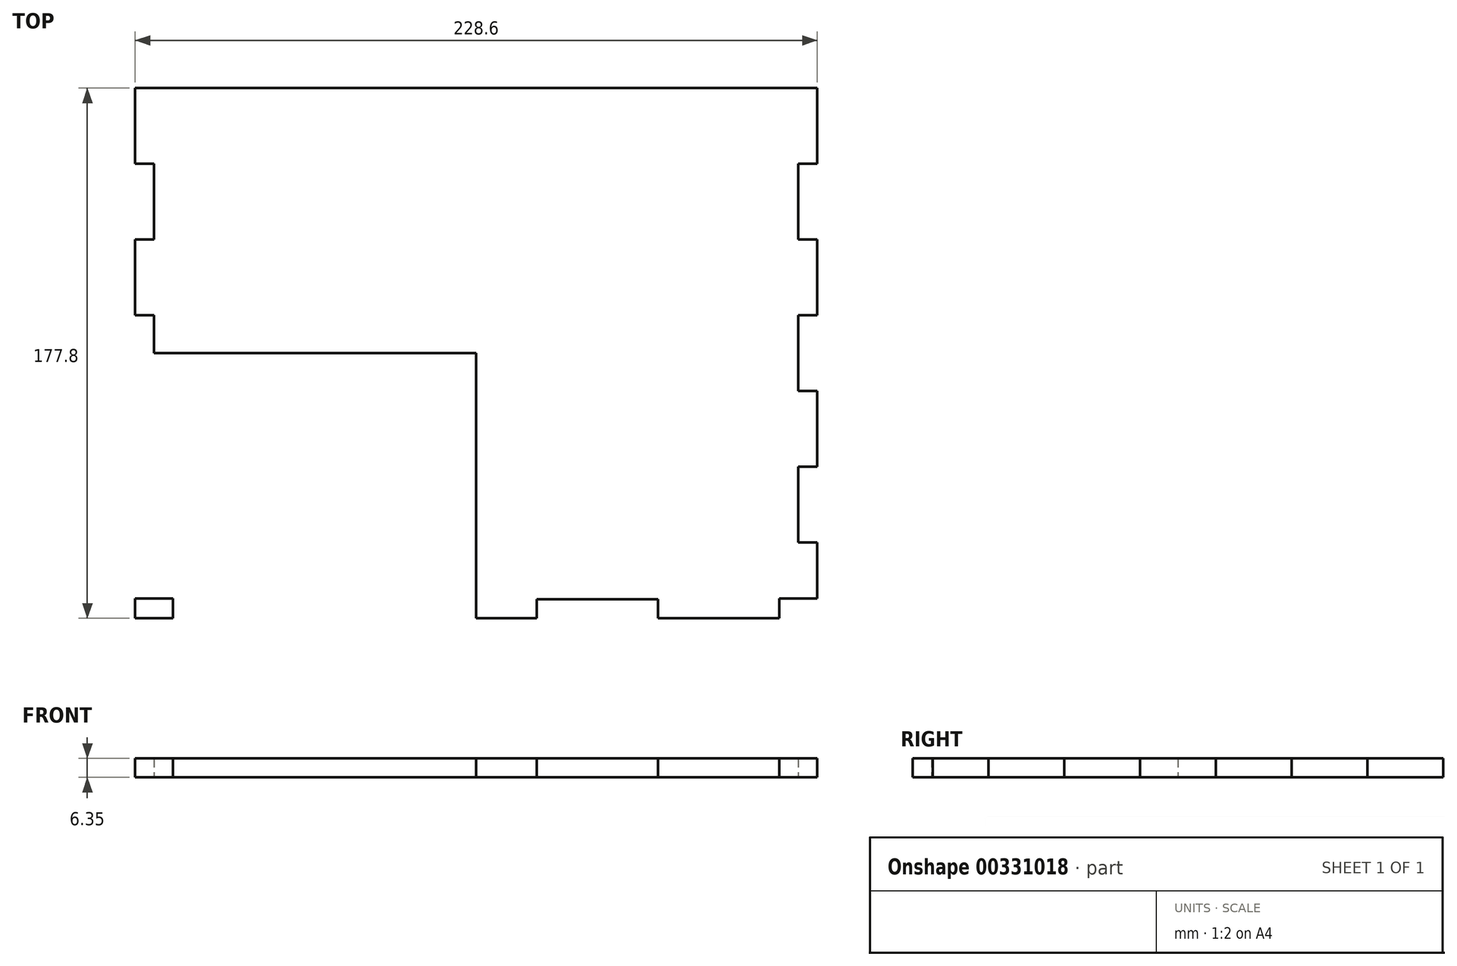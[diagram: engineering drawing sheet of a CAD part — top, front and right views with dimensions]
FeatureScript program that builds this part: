
annotation { "Feature Type Name" : "Feature", "Feature Type Description" : "" }
export const myFeature = defineFeature(function(context is Context, id is Id, definition is map)
    precondition{}
    {
        {
            var Q0;
            Q0=qCreatedBy(makeId("Top.planeOp"),FACE);
            var sketch = newSketch(context, id + "F0", { "sketchPlane" : qUnion([Q0])});
            skLineSegment(sketch, "E0.bottom", {"start": v(114.3, 88.9) * mm, "end": v(-114.3, 88.9) * mm});
            skLineSegment(sketch, "E0.top", {"start": v(114.3, -88.9) * mm, "end": v(-114.3, -88.9) * mm});
            skLineSegment(sketch, "E0.left", {"start": v(114.3, 88.9) * mm, "end": v(114.3, -88.9) * mm});
            skLineSegment(sketch, "E0.right", {"start": v(-114.3, 88.9) * mm, "end": v(-114.3, -88.9) * mm});
            skPoint(sketch, "E0.middle", {"position": v(0, 0) * mm});
            skLineSegment(sketch, "E1", {"start": v(-114.3, 88.9) * mm, "end": v(-114.3, 82.55) * mm});
            skLineSegment(sketch, "E2", {"start": v(-114.3, 88.9) * mm, "end": v(-101.6, 88.9) * mm});
            skLineSegment(sketch, "E3.bottom", {"start": v(-101.6, 88.9) * mm, "end": v(-114.3, 88.9) * mm});
            skLineSegment(sketch, "E3.top", {"start": v(-101.6, 82.55) * mm, "end": v(-114.3, 82.55) * mm});
            skLineSegment(sketch, "E3.left", {"start": v(-101.6, 88.9) * mm, "end": v(-101.6, 82.55) * mm});
            skLineSegment(sketch, "E4", {"start": v(-114.3, 88.9) * mm, "end": v(-114.3, 63.5) * mm});
            skLineSegment(sketch, "E5.bottom", {"start": v(-114.3, 63.5) * mm, "end": v(-107.95, 63.5) * mm});
            skLineSegment(sketch, "E5.top", {"start": v(-114.3, 38.1) * mm, "end": v(-107.95, 38.1) * mm});
            skLineSegment(sketch, "E5.left", {"start": v(-114.3, 63.5) * mm, "end": v(-114.3, 38.1) * mm});
            skLineSegment(sketch, "E5.right", {"start": v(-107.95, 63.5) * mm, "end": v(-107.95, 38.1) * mm});
            skLineSegment(sketch, "E6", {"start": v(-114.3, 38.1) * mm, "end": v(-114.3, 12.7) * mm});
            skLineSegment(sketch, "E7.bottom", {"start": v(-114.3, 12.7) * mm, "end": v(-107.95, 12.7) * mm});
            skLineSegment(sketch, "E7.top", {"start": v(-114.3, -12.7) * mm, "end": v(-107.95, -12.7) * mm});
            skLineSegment(sketch, "E7.left", {"start": v(-114.3, 12.7) * mm, "end": v(-114.3, -12.7) * mm});
            skLineSegment(sketch, "E7.right", {"start": v(-107.95, 12.7) * mm, "end": v(-107.95, -12.7) * mm});
            skLineSegment(sketch, "E8", {"start": v(-114.3, -12.7) * mm, "end": v(-114.3, -38.1) * mm});
            skLineSegment(sketch, "E9.bottom", {"start": v(-114.3, -38.1) * mm, "end": v(-107.95, -38.1) * mm});
            skLineSegment(sketch, "E9.top", {"start": v(-114.3, -63.5) * mm, "end": v(-107.95, -63.5) * mm});
            skLineSegment(sketch, "E9.left", {"start": v(-114.3, -38.1) * mm, "end": v(-114.3, -63.5) * mm});
            skLineSegment(sketch, "E9.right", {"start": v(-107.95, -38.1) * mm, "end": v(-107.95, -63.5) * mm});
            skLineSegment(sketch, "E10", {"start": v(-114.3, -88.9) * mm, "end": v(-114.3, -82.55) * mm});
            skLineSegment(sketch, "E11.bottom", {"start": v(-114.3, -88.9) * mm, "end": v(-101.6, -88.9) * mm});
            skLineSegment(sketch, "E11.top", {"start": v(-114.3, -82.26) * mm, "end": v(-101.6, -82.26) * mm});
            skLineSegment(sketch, "E11.left", {"start": v(-114.3, -88.9) * mm, "end": v(-114.3, -82.26) * mm});
            skLineSegment(sketch, "E11.right", {"start": v(-101.6, -88.9) * mm, "end": v(-101.6, -82.26) * mm});
            skLineSegment(sketch, "E12", {"start": v(0, 88.9) * mm, "end": v(0, -88.9) * mm});
            skLineSegment(sketch, "E13.MirrorCS", {"start": v(101.6, 88.9) * mm, "end": v(114.3, 88.9) * mm});
            skLineSegment(sketch, "E14.MirrorCS", {"start": v(101.6, 88.9) * mm, "end": v(101.6, 82.55) * mm});
            skLineSegment(sketch, "E15.MirrorCS", {"start": v(101.6, 82.55) * mm, "end": v(114.3, 82.55) * mm});
            skLineSegment(sketch, "E16.MirrorCS", {"start": v(114.3, 88.9) * mm, "end": v(114.3, 63.5) * mm});
            skLineSegment(sketch, "E17.MirrorCS", {"start": v(114.3, 63.5) * mm, "end": v(107.95, 63.5) * mm});
            skLineSegment(sketch, "E18.MirrorCS", {"start": v(107.95, 63.5) * mm, "end": v(107.95, 38.1) * mm});
            skLineSegment(sketch, "E19.MirrorCS", {"start": v(114.3, 38.1) * mm, "end": v(107.95, 38.1) * mm});
            skLineSegment(sketch, "E20.MirrorCS", {"start": v(114.3, 12.7) * mm, "end": v(107.95, 12.7) * mm});
            skLineSegment(sketch, "E21.MirrorCS", {"start": v(107.95, 12.7) * mm, "end": v(107.95, -12.7) * mm});
            skLineSegment(sketch, "E22.MirrorCS", {"start": v(114.3, -12.7) * mm, "end": v(107.95, -12.7) * mm});
            skLineSegment(sketch, "E23.MirrorCS", {"start": v(114.3, -38.1) * mm, "end": v(107.95, -38.1) * mm});
            skLineSegment(sketch, "E24.MirrorCS", {"start": v(107.95, -38.1) * mm, "end": v(107.95, -63.5) * mm});
            skLineSegment(sketch, "E25.MirrorCS", {"start": v(114.3, -63.5) * mm, "end": v(107.95, -63.5) * mm});
            skLineSegment(sketch, "E26.MirrorCS", {"start": v(114.3, -82.26) * mm, "end": v(101.6, -82.26) * mm});
            skLineSegment(sketch, "E27.MirrorCS", {"start": v(101.6, -88.9) * mm, "end": v(101.6, -82.26) * mm});
            skLineSegment(sketch, "E28.MirrorCS", {"start": v(-114.3, -88.9) * mm, "end": v(114.3, -88.9) * mm});
            skLineSegment(sketch, "E29", {"start": v(-114.3, 0) * mm, "end": v(114.3, 0) * mm});
            skLineSegment(sketch, "E30", {"start": v(-101.6, 88.9) * mm, "end": v(-60.96, 88.9) * mm});
            skLineSegment(sketch, "E31.bottom", {"start": v(-60.96, 88.9) * mm, "end": v(-20.32, 88.9) * mm});
            skLineSegment(sketch, "E31.top", {"start": v(-60.96, 82.55) * mm, "end": v(-20.32, 82.55) * mm});
            skLineSegment(sketch, "E31.left", {"start": v(-60.96, 88.9) * mm, "end": v(-60.96, 82.55) * mm});
            skLineSegment(sketch, "E31.right", {"start": v(-20.32, 88.9) * mm, "end": v(-20.32, 82.55) * mm});
            skLineSegment(sketch, "E32", {"start": v(-20.32, 88.9) * mm, "end": v(20.32, 88.9) * mm});
            skLineSegment(sketch, "E33.bottom", {"start": v(20.32, 88.9) * mm, "end": v(60.96, 88.9) * mm});
            skLineSegment(sketch, "E33.top", {"start": v(20.32, 82.55) * mm, "end": v(60.96, 82.55) * mm});
            skLineSegment(sketch, "E33.left", {"start": v(20.32, 88.9) * mm, "end": v(20.32, 82.55) * mm});
            skLineSegment(sketch, "E33.right", {"start": v(60.96, 88.9) * mm, "end": v(60.96, 82.55) * mm});
            skLineSegment(sketch, "E34.MirrorCS", {"start": v(-101.6, -88.9) * mm, "end": v(-60.96, -88.9) * mm});
            skLineSegment(sketch, "E35.MirrorCS", {"start": v(-60.96, -88.9) * mm, "end": v(-60.96, -82.55) * mm});
            skLineSegment(sketch, "E36.MirrorCS", {"start": v(-60.96, -88.9) * mm, "end": v(-20.32, -88.9) * mm});
            skLineSegment(sketch, "E37.MirrorCS", {"start": v(-60.96, -82.55) * mm, "end": v(-20.32, -82.55) * mm});
            skLineSegment(sketch, "E38.MirrorCS", {"start": v(-20.32, -88.9) * mm, "end": v(-20.32, -82.55) * mm});
            skLineSegment(sketch, "E39.MirrorCS", {"start": v(20.32, -82.55) * mm, "end": v(60.96, -82.55) * mm});
            skLineSegment(sketch, "E40.MirrorCS", {"start": v(60.96, -88.9) * mm, "end": v(60.96, -82.55) * mm});
            skLineSegment(sketch, "E41.MirrorCS", {"start": v(101.6, -88.9) * mm, "end": v(101.6, -82.55) * mm});
            skLineSegment(sketch, "E42.MirrorCS", {"start": v(20.32, -88.9) * mm, "end": v(20.32, -82.55) * mm});
            skSolve(sketch);
        }
        {
            var Q0;
            {var subQ8=sQuery(id+"F0.wireOp",EDGE,"E3.top");Q0=makeQuery(id+"F0.imprint","IMPRINT",FACE,{"disambiguationData":[TD([[makeQuery(id+"F0.imprint","IMPRINT",EDGE,{"derivedFrom":subQ8}),1.0]])]});}
            var Q1;
            Q1=makeQuery(id+"F0.imprint","IMPRINT",FACE,{"disambiguationData":[TD([[makeQuery(id+"F0.imprint","IMPRINT",EDGE,{"derivedFrom":sQuery(id+"F0.wireOp",EDGE,"E0.bottom")}),1.0]])]});
            var Q2;
            {var subQ8=sQuery(id+"F0.wireOp",EDGE,"E22.MirrorCS");Q2=makeQuery(id+"F0.imprint","IMPRINT",FACE,{"disambiguationData":[TD([[makeQuery(id+"F0.imprint","IMPRINT",EDGE,{"derivedFrom":subQ8}),1.0]])]});}
            var Q3;
            Q3=makeQuery(id+"F0.imprint","IMPRINT",FACE,{"disambiguationData":[TD([[makeQuery(id+"F0.imprint","IMPRINT",EDGE,{"derivedFrom":sQuery(id+"F0.wireOp",EDGE,"E0.right")}),1.0]])]});
            extrude(context, id + "F1", {"entities" : qUnion([Q0, Q1, Q2, Q3]), "depth" : 6.35 * mm});
        }
    });
